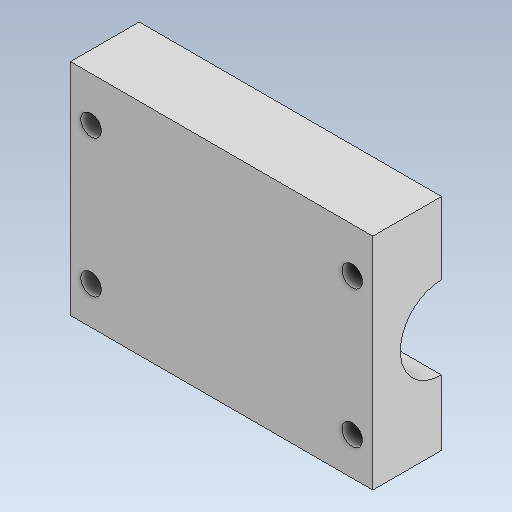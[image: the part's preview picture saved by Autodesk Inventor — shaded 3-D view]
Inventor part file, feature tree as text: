
AUTODESK INVENTOR PART (.ipt)
format: ipt  version: 2020 (Build 240168000, 168)  size: 109,568 bytes
history: native  units: in
note: dims shown in document units (in); Inventor stores cm internally (conversion verified against a paired STEP export)
features: reference x6, other x3, extrude x2, sketch x2
ambient origin geometry x8: Origin, YZ Plane, XZ Plane, XY Plane, X Axis, Y Axis, Z Axis, Center Point
bodies: Solid1 (feature_tree)
feature tree (13):
  extrude  "Extrusion1"  Depth=0.625in TaperAngle=0.0deg
  extrude  "Extrusion2"  [1 undecoded]
  sketch  "Sketch1"  dims[d0=2.0in d1=0.625in d2=0.0in]
  reference  "Reference1"
  reference  "Reference2"
  reference  "Reference3"
  reference  "Reference4"
  reference  "Reference5"
  sketch  "Sketch2"  dims[d3=3.0in d4=0.0in]
  reference  "Reference6"
  other  "<userpath>\Desktop\PnP Machine\PnP Machine.iam"
  other  "PnP Machine.iam"
  other  "YClamp:1"
note: 1 required parameter value undecoded (feature->parameter linkage not recoverable at this tier; creation-order binding heuristic only, values carry confidence <= 0.55)
